# Revit family: Rohrschelle Omnia MB, M10-M12, Silikon
name_source: partatom
category: HLS-Bauteile
revit_build: Autodesk Revit 2017 (Build: 20190507_1515(x64)
units: mm (PartAtom-declared; Revit-internal decimal feet)

## family parameters
Arbeitsebenenbasiert = Ja
Beim Laden mit Abzugskörper schneiden = Nein
Bemaßung runder Anschluss = Durchmesser verwenden
Gemeinsam genutzt = Ja
Immer vertikal = Nein
Raumberechnungspunkt = Nein
Teiletyp = Normal

## types (4) — shared parameters
A = 30 mm  [stored 0.0984252 ft]
AB = 4 mm  [stored 0.0131234 ft]
Anschluss = M10/M12
Anschlußhöhe = 30 mm
BP = 16 mm  [stored 0.0524934 ft]
Bauart = zweiteilig
Baustoffklasse = B2
Brandschutz = RAL GZ 656
DF1 = 19 mm  [stored 0.062336 ft]
DF2 = 19 mm  [stored 0.062336 ft]
DS = 6 mm  [stored 0.019685 ft]
DVS = 7 mm  [stored 0.0229659 ft]
Dämmstärke = 6 mm  [stored 0.019685 ft]
Fabrikat = MEFA
Farbe Schalldämmeinlage = rot
Firma = MEFA Befestigungs- und Montagesysteme GmbH
HGA = 21 mm  [stored 0.0688976 ft]
Kurztext1 = Rohrschelle Omnia MB 25x3,0
L Ü Bogen = 20 mm  [stored 0.0656168 ft]
MB = 25 mm  [stored 0.082021 ft]
MD = 3 mm  [stored 0.00984252 ft]
Material = Stahl
Material Schalldämmeinlage = Silikon
Materialmaße = 25x3,0 mm
Materialname = DD11
Mengeneinheit = St
Oberflaeche = galvanisch verzinkt
Schalldämmeinlage = Silikon
Verschluss = Schwenkbarer U-Verschluss
Verschluss-Schraube = M8
Vorgabe-Ansicht = 1219 mm
d1 = 7 mm  [stored 0.0229659 ft]
max. Temperaturbeständigkeit = 250 °C
max. zul. Last = 2.30 kN
max. zul. Last horizontal = 0.00 kN
max. zul. Last vertikal = 0.00 kN
vpe = 25 St
zero-valued in all types: Nennweite DN Rohr, Rohraußendurchmesser, Stärke Material

## per-type parameters (varying)
| type | Artikelnummer | B | Breite | D | D0 | Dmax | Dmin | EAN | Gewicht | Gewicht pro Bauteil | H | Kurztext2 | R | RM | Rohraußendurchmesser Zoll | S | S1 | max. Höhe | max. Rohraußendurchmesser | min. Rohraußendurchmesser |
| Omnia MB, Ø132-136, M10/M12, Silikon | 1418336 | 192 mm  [stored 0.629921 ft] | 192 mm  [stored 0.629921 ft] | 136 mm | 148 mm  [stored 0.485564 ft] | 136 mm | 132 mm  [stored 0.433071 ft] | 4250928424884 | 0.45 kg | 0.45 kg | 175 mm  [stored 0.574147 ft] | 132 - 136 mm M10/M12 Silikon | 74 mm  [stored 0.242782 ft] | 77 mm  [stored 0.252625 ft] | Zoll | 173 mm  [stored 0.567585 ft] | 168 mm  [stored 0.551181 ft] | 175 mm  [stored 0.574147 ft] | 136 mm | 132 mm  [stored 0.433071 ft] |
| Omnia MB, Ø137-141, M10/M12, Silikon | 1418341 | 197 mm | 197 mm | 141 mm  [stored 0.462598 ft] | 153 mm  [stored 0.501969 ft] | 141 mm  [stored 0.462598 ft] | 137 mm  [stored 0.449475 ft] | 4250928424891 | 0.46 kg | 0.46 kg | 180 mm  [stored 0.590551 ft] | 137 - 141 mm M10/M12 Silikon | 77 mm  [stored 0.252625 ft] | 80 mm | 5 Zoll | 178 mm  [stored 0.58399 ft] | 173 mm  [stored 0.567585 ft] | 180 mm  [stored 0.590551 ft] | 141 mm  [stored 0.462598 ft] | 137 mm  [stored 0.449475 ft] |
| Omnia MB, Ø159-163, M10/M12, Silikon | 1418363 | 219 mm  [stored 0.718504 ft] | 219 mm  [stored 0.718504 ft] | 163 mm  [stored 0.534777 ft] | 175 mm  [stored 0.574147 ft] | 163 mm  [stored 0.534777 ft] | 159 mm  [stored 0.521654 ft] | 4250928424907 | 0.51 kg | 0.51 kg | 202 mm  [stored 0.66273 ft] | 159 - 163 mm M10/M12 Silikon | 88 mm | 91 mm | Zoll | 200 mm  [stored 0.656168 ft] | 195 mm  [stored 0.639764 ft] | 197 mm | 163 mm  [stored 0.534777 ft] | 159 mm  [stored 0.521654 ft] |
| Omnia MB, Ø164-168, M10/M12, Silikon | 1418368 | 224 mm | 225 mm | 168 mm  [stored 0.551181 ft] | 180 mm  [stored 0.590551 ft] | 168 mm  [stored 0.551181 ft] | 164 mm  [stored 0.538058 ft] | 4250928424914 | 0.53 kg | 0.53 kg | 207 mm  [stored 0.679134 ft] | 164 - 168 mm M10/M12 Silikon | 90 mm | 93 mm  [stored 0.305118 ft] | 6 Zoll | 205 mm | 200 mm  [stored 0.656168 ft] | 202 mm  [stored 0.66273 ft] | 168 mm  [stored 0.551181 ft] | 164 mm  [stored 0.538058 ft] |

note: [stored X ft] marks values corroborated as IEEE doubles in the binary element streams (Revit-internal decimal feet)

## geometry (parser evidence)
native form markers: Sweep x3
no freeform markers — native parametric forms only
